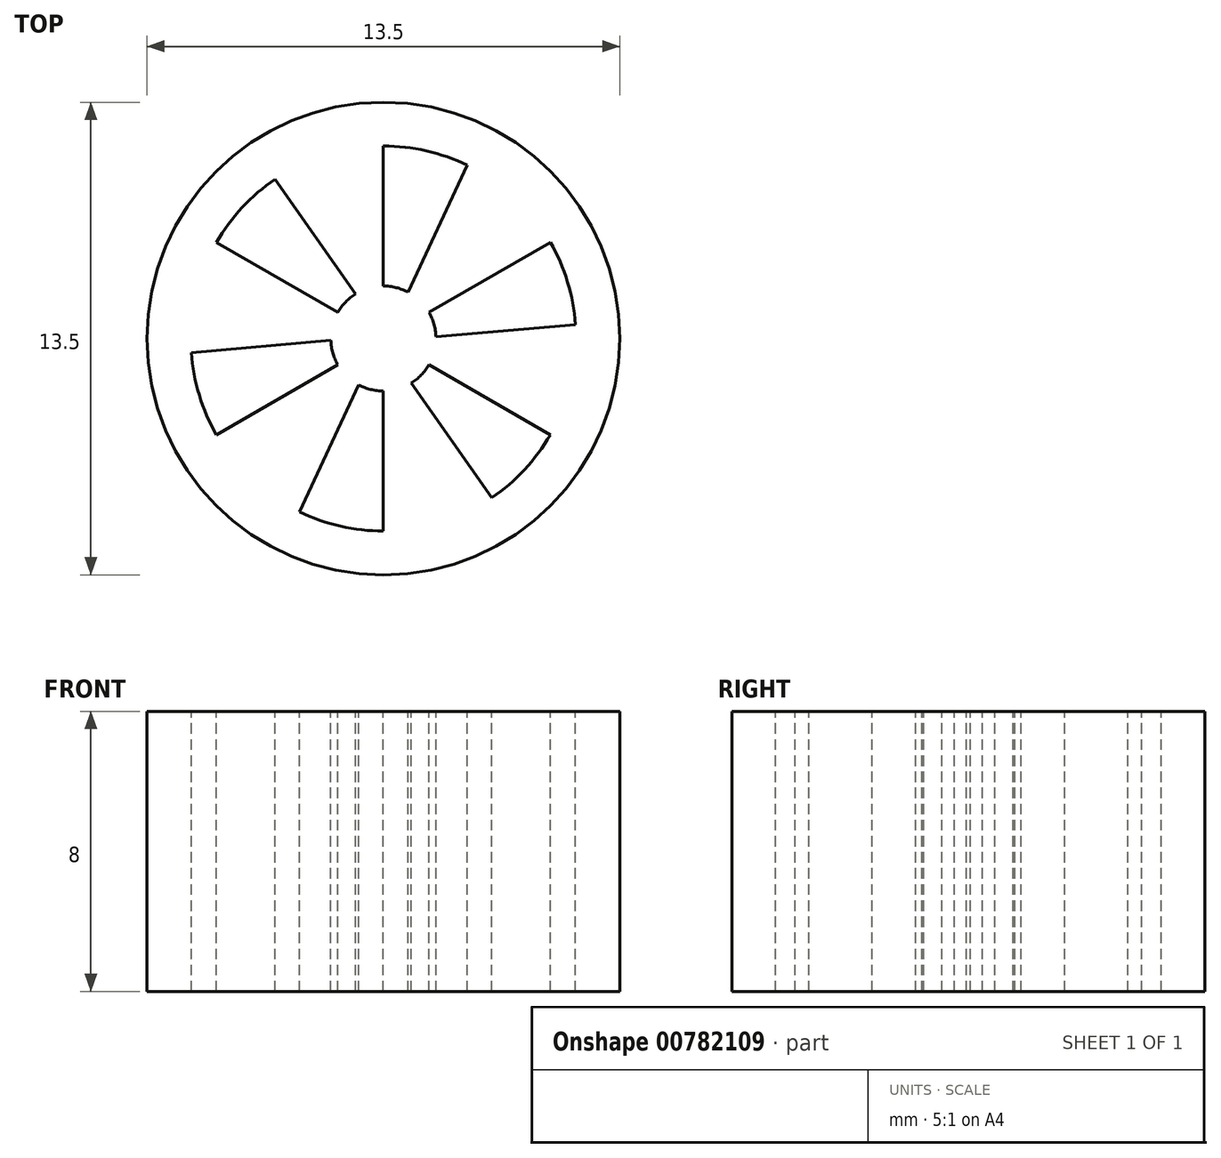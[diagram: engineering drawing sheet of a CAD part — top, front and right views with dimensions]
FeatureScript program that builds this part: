
annotation { "Feature Type Name" : "Feature", "Feature Type Description" : "" }
export const myFeature = defineFeature(function(context is Context, id is Id, definition is map)
    precondition{}
    {
        {
            var Q0;
            Q0=qCreatedBy(makeId("Top.planeOp"),FACE);
            var sketch = newSketch(context, id + "F0", { "sketchPlane" : qUnion([Q0])});
            skCircle(sketch, "E0", {"center": v(0, 0) * mm, "radius": 6.75 * mm});
            skSolve(sketch);
        }
        {
            var Q0;
            Q0=makeQuery(id+"F0.imprint","IMPRINT",FACE,{"disambiguationData":[TD([[makeQuery(id+"F0.imprint","IMPRINT",EDGE,{"derivedFrom":sQuery(id+"F0.wireOp",EDGE,"E0")}),1.0]])]});
            extrude(context, id + "F1", {"entities" : qUnion([Q0]), "depth" : 8 * mm, "offsetDistance" : 25 * mm});
        }
        {
            var Q0;
            Q0=makeQuery(id+"F1.opExtrude","CAP_FACE",FACE,{"disambiguationData":[OSD([sQuery(id+"F0.wireOp",EDGE,"E0")])],"isStart":false});
            var sketch = newSketch(context, id + "F2", { "sketchPlane" : qUnion([Q0])});
            skCircle(sketch, "E1", {"center": v(0, 0) * mm, "radius": 1.5 * mm});
            skCircle(sketch, "E2", {"center": v(0, 0) * mm, "radius": 5.5 * mm});
            skLineSegment(sketch, "E3", {"start": v(0, 1.5) * mm, "end": v(0, 5.5) * mm});
            skLineSegment(sketch, "E4", {"start": v(0.7, 1.32) * mm, "end": v(2.4, 4.95) * mm});
            skLineSegment(sketch, "E5.1.0", {"start": v(-0.8, 1.27) * mm, "end": v(-3.09, 4.55) * mm});
            skLineSegment(sketch, "E5.1.1", {"start": v(-1.3, 0.75) * mm, "end": v(-4.76, 2.75) * mm});
            skLineSegment(sketch, "E5.2.0", {"start": v(-1.5, -0.05) * mm, "end": v(-5.49, -0.4) * mm});
            skLineSegment(sketch, "E5.2.1", {"start": v(-1.3, -0.75) * mm, "end": v(-4.76, -2.75) * mm});
            skLineSegment(sketch, "E5.3.0", {"start": v(-0.7, -1.32) * mm, "end": v(-2.4, -4.95) * mm});
            skLineSegment(sketch, "E5.3.1", {"start": v(0, -1.5) * mm, "end": v(0, -5.5) * mm});
            skLineSegment(sketch, "E5.4.0", {"start": v(0.8, -1.27) * mm, "end": v(3.09, -4.55) * mm});
            skLineSegment(sketch, "E5.4.1", {"start": v(1.3, -0.75) * mm, "end": v(4.76, -2.75) * mm});
            skLineSegment(sketch, "E5.5.0", {"start": v(1.5, 0.05) * mm, "end": v(5.49, 0.4) * mm});
            skLineSegment(sketch, "E5.5.1", {"start": v(1.3, 0.75) * mm, "end": v(4.76, 2.75) * mm});
            skSolve(sketch);
        }
        {
            var Q0;
            {var subQ0=sQuery(id+"F2.wireOp",EDGE,"E3");Q0=makeQuery(id+"F2.imprint","IMPRINT",FACE,{"disambiguationData":[TD([[makeQuery(id+"F2.imprint","IMPRINT",EDGE,{"derivedFrom":subQ0}),-1.0]])]});}
            var Q1;
            {var subQ0=sQuery(id+"F2.wireOp",EDGE,"E5.5.0");Q1=makeQuery(id+"F2.imprint","IMPRINT",FACE,{"disambiguationData":[TD([[makeQuery(id+"F2.imprint","IMPRINT",EDGE,{"derivedFrom":subQ0}),1.0]])]});}
            var Q2;
            {var subQ0=sQuery(id+"F2.wireOp",EDGE,"E5.4.0");Q2=makeQuery(id+"F2.imprint","IMPRINT",FACE,{"disambiguationData":[TD([[makeQuery(id+"F2.imprint","IMPRINT",EDGE,{"derivedFrom":subQ0}),1.0]])]});}
            var Q3;
            {var subQ0=sQuery(id+"F2.wireOp",EDGE,"E5.3.0");Q3=makeQuery(id+"F2.imprint","IMPRINT",FACE,{"disambiguationData":[TD([[makeQuery(id+"F2.imprint","IMPRINT",EDGE,{"derivedFrom":subQ0}),1.0]])]});}
            var Q4;
            {var subQ0=sQuery(id+"F2.wireOp",EDGE,"E5.2.0");Q4=makeQuery(id+"F2.imprint","IMPRINT",FACE,{"disambiguationData":[TD([[makeQuery(id+"F2.imprint","IMPRINT",EDGE,{"derivedFrom":subQ0}),1.0]])]});}
            var Q5;
            {var subQ0=sQuery(id+"F2.wireOp",EDGE,"E5.1.0");Q5=makeQuery(id+"F2.imprint","IMPRINT",FACE,{"disambiguationData":[TD([[makeQuery(id+"F2.imprint","IMPRINT",EDGE,{"derivedFrom":subQ0}),1.0]])]});}
            extrude(context, id + "F3", {"entities" : qUnion([Q0, Q1, Q2, Q3, Q4, Q5]), "operationType" : NewBodyOperationType.REMOVE, "oppositeDirection" : true, "depth" : 25 * mm, "offsetDistance" : 25 * mm});
        }
    });
